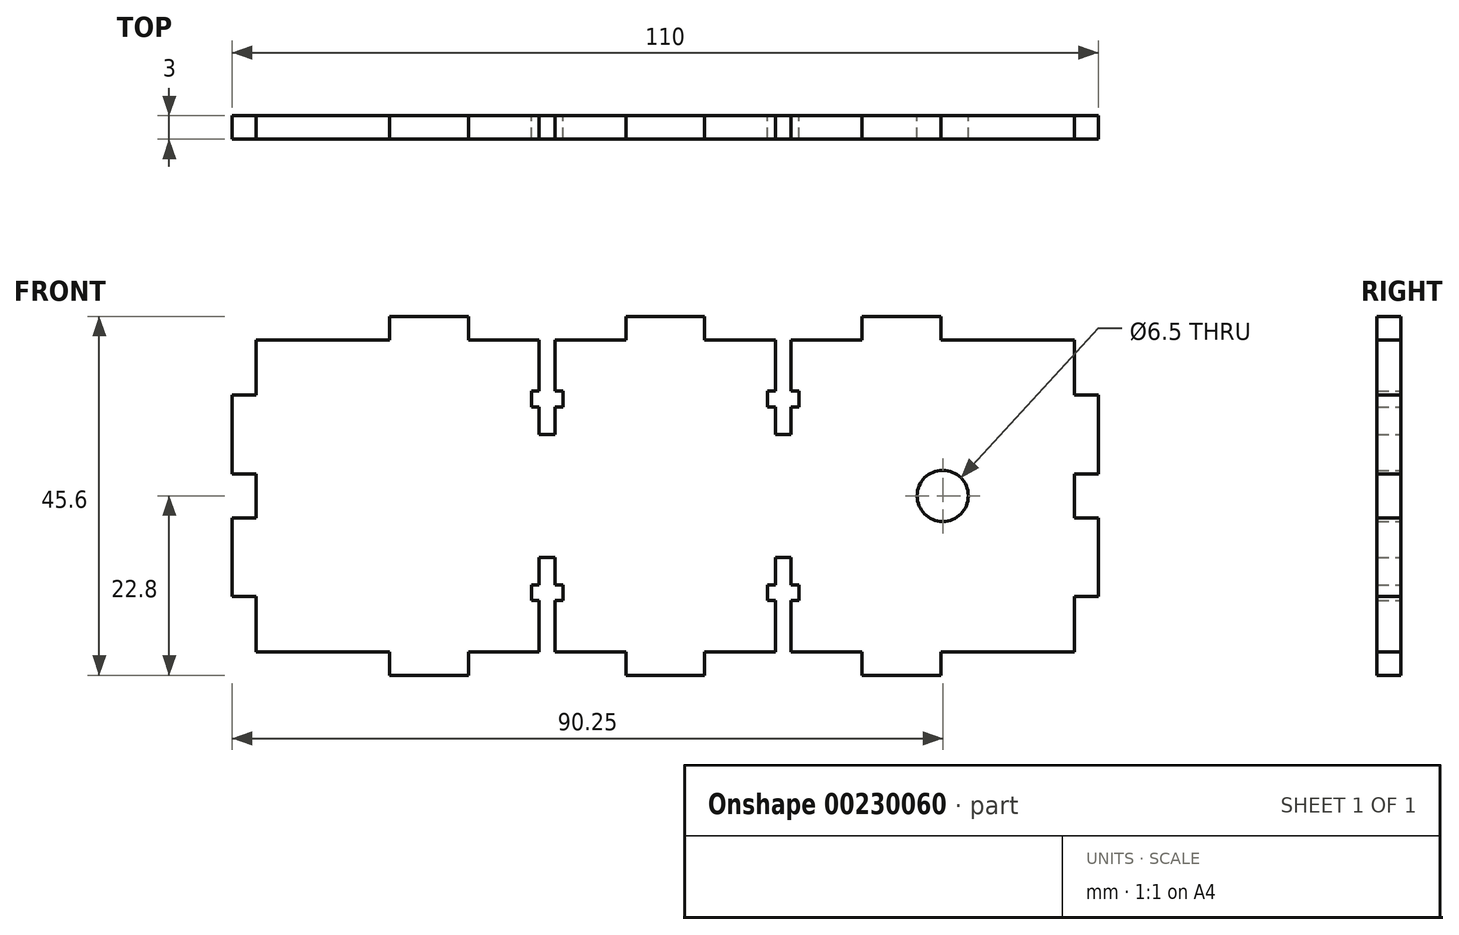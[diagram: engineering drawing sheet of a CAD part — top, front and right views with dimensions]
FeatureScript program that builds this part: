
annotation { "Feature Type Name" : "Feature", "Feature Type Description" : "" }
export const myFeature = defineFeature(function(context is Context, id is Id, definition is map)
    precondition{}
    {
        {
            var Q0;
            Q0=qCreatedBy(makeId("Front.planeOp"),FACE);
            var sketch = newSketch(context, id + "F0", { "sketchPlane" : qUnion([Q0])});
            skLineSegment(sketch, "E0", {"start": v(3, 0) * mm, "end": v(0, 0) * mm});
            skLineSegment(sketch, "E1", {"start": v(3, 0) * mm, "end": v(3, 2.8) * mm});
            skLineSegment(sketch, "E2", {"start": v(3, 2.8) * mm, "end": v(0, 2.8) * mm});
            skLineSegment(sketch, "E3", {"start": v(0, 2.8) * mm, "end": v(0, 12.8) * mm});
            skLineSegment(sketch, "E4", {"start": v(0, 12.8) * mm, "end": v(3, 12.8) * mm});
            skLineSegment(sketch, "E5", {"start": v(3, 12.8) * mm, "end": v(3, 19.8) * mm});
            skLineSegment(sketch, "E6", {"start": v(3, 19.8) * mm, "end": v(20, 19.8) * mm});
            skLineSegment(sketch, "E7", {"start": v(20, 19.8) * mm, "end": v(20, 22.8) * mm});
            skLineSegment(sketch, "E8", {"start": v(20, 22.8) * mm, "end": v(30, 22.8) * mm});
            skLineSegment(sketch, "E9", {"start": v(30, 22.8) * mm, "end": v(30, 19.8) * mm});
            skLineSegment(sketch, "E10", {"start": v(30, 19.8) * mm, "end": v(39, 19.8) * mm});
            skLineSegment(sketch, "E11", {"start": v(50, 19.8) * mm, "end": v(50, 22.8) * mm});
            skLineSegment(sketch, "E12", {"start": v(50, 22.8) * mm, "end": v(55, 22.8) * mm});
            skLineSegment(sketch, "E13", {"start": v(40, 13.3) * mm, "end": v(40, 0) * mm, "construction": true});
            skLineSegment(sketch, "E14.top", {"start": v(39, 7.8) * mm, "end": v(41, 7.8) * mm});
            skLineSegment(sketch, "E14.left", {"start": v(39, 19.8) * mm, "end": v(39, 13.3) * mm});
            skLineSegment(sketch, "E14.right", {"start": v(41, 19.8) * mm, "end": v(41, 13.3) * mm});
            skLineSegment(sketch, "E15.bottom", {"start": v(38, 13.3) * mm, "end": v(39, 13.3) * mm});
            skLineSegment(sketch, "E15.top", {"start": v(38, 11.3) * mm, "end": v(39, 11.3) * mm});
            skLineSegment(sketch, "E15.left", {"start": v(38, 13.3) * mm, "end": v(38, 11.3) * mm});
            skLineSegment(sketch, "E15.right", {"start": v(42, 13.3) * mm, "end": v(42, 11.3) * mm});
            skPoint(sketch, "E16.orphan", {"position": v(40, 19.8) * mm});
            skLineSegment(sketch, "E17.trimOffspring", {"start": v(41, 19.8) * mm, "end": v(50, 19.8) * mm});
            skLineSegment(sketch, "E18.trimOffspring", {"start": v(41, 13.3) * mm, "end": v(42, 13.3) * mm});
            skLineSegment(sketch, "E19.trimOffspring", {"start": v(41, 11.3) * mm, "end": v(41, 7.8) * mm});
            skLineSegment(sketch, "E20.trimOffspring", {"start": v(39, 11.3) * mm, "end": v(39, 7.8) * mm});
            skLineSegment(sketch, "E21.trimOffspring", {"start": v(41, 11.3) * mm, "end": v(42, 11.3) * mm});
            skLineSegment(sketch, "E22", {"start": v(55, 0) * mm, "end": v(3, 0) * mm, "construction": true});
            skLineSegment(sketch, "E23.MirrorCS", {"start": v(38, -11.3) * mm, "end": v(39, -11.3) * mm});
            skLineSegment(sketch, "E24.MirrorCS", {"start": v(41, -13.3) * mm, "end": v(42, -13.3) * mm});
            skLineSegment(sketch, "E25.MirrorCS", {"start": v(41, -11.3) * mm, "end": v(42, -11.3) * mm});
            skLineSegment(sketch, "E26.MirrorCS", {"start": v(38, -13.3) * mm, "end": v(39, -13.3) * mm});
            skLineSegment(sketch, "E27.MirrorCS", {"start": v(39, -7.8) * mm, "end": v(41, -7.8) * mm});
            skLineSegment(sketch, "E28.MirrorCS", {"start": v(3, 0) * mm, "end": v(3, -2.8) * mm});
            skLineSegment(sketch, "E29.MirrorCS", {"start": v(38, -13.3) * mm, "end": v(38, -11.3) * mm});
            skLineSegment(sketch, "E30.MirrorCS", {"start": v(41, -19.8) * mm, "end": v(41, -13.3) * mm});
            skLineSegment(sketch, "E31.MirrorCS", {"start": v(50, -19.8) * mm, "end": v(50, -22.8) * mm});
            skLineSegment(sketch, "E32.MirrorCS", {"start": v(50, -22.8) * mm, "end": v(55, -22.8) * mm});
            skLineSegment(sketch, "E33.MirrorCS", {"start": v(30, -19.8) * mm, "end": v(39, -19.8) * mm});
            skLineSegment(sketch, "E34.MirrorCS", {"start": v(42, -13.3) * mm, "end": v(42, -11.3) * mm});
            skLineSegment(sketch, "E35.MirrorCS", {"start": v(30, -22.8) * mm, "end": v(30, -19.8) * mm});
            skLineSegment(sketch, "E36.MirrorCS", {"start": v(20, -22.8) * mm, "end": v(30, -22.8) * mm});
            skLineSegment(sketch, "E37.MirrorCS", {"start": v(20, -19.8) * mm, "end": v(20, -22.8) * mm});
            skLineSegment(sketch, "E38.MirrorCS", {"start": v(3, -2.8) * mm, "end": v(0, -2.8) * mm});
            skLineSegment(sketch, "E39.MirrorCS", {"start": v(0, -2.8) * mm, "end": v(0, -12.8) * mm});
            skLineSegment(sketch, "E40.MirrorCS", {"start": v(41, -19.8) * mm, "end": v(50, -19.8) * mm});
            skLineSegment(sketch, "E41.MirrorCS", {"start": v(3, -12.8) * mm, "end": v(3, -19.8) * mm});
            skLineSegment(sketch, "E42.MirrorCS", {"start": v(39, -11.3) * mm, "end": v(39, -7.8) * mm});
            skLineSegment(sketch, "E43.MirrorCS", {"start": v(0, -12.8) * mm, "end": v(3, -12.8) * mm});
            skLineSegment(sketch, "E44.MirrorCS", {"start": v(3, -19.8) * mm, "end": v(20, -19.8) * mm});
            skLineSegment(sketch, "E45.MirrorCS", {"start": v(41, -11.3) * mm, "end": v(41, -7.8) * mm});
            skLineSegment(sketch, "E46.MirrorCS", {"start": v(39, -19.8) * mm, "end": v(39, -13.3) * mm});
            skLineSegment(sketch, "E47.MirrorCS", {"start": v(40, -13.3) * mm, "end": v(40, 0) * mm, "construction": true});
            skPoint(sketch, "E48.MirrorP", {"position": v(40, -19.8) * mm});
            skLineSegment(sketch, "E49", {"start": v(55, 22.8) * mm, "end": v(55, -22.8) * mm, "construction": true});
            skLineSegment(sketch, "E50.MirrorCS", {"start": v(72, -13.3) * mm, "end": v(71, -13.3) * mm});
            skLineSegment(sketch, "E51.MirrorCS", {"start": v(72, 13.3) * mm, "end": v(71, 13.3) * mm});
            skLineSegment(sketch, "E52.MirrorCS", {"start": v(72, -13.3) * mm, "end": v(72, -11.3) * mm});
            skLineSegment(sketch, "E53.MirrorCS", {"start": v(71, 7.8) * mm, "end": v(69, 7.8) * mm});
            skLineSegment(sketch, "E54.MirrorCS", {"start": v(107, 0) * mm, "end": v(110, 0) * mm});
            skLineSegment(sketch, "E55.MirrorCS", {"start": v(72, -11.3) * mm, "end": v(71, -11.3) * mm});
            skLineSegment(sketch, "E56.MirrorCS", {"start": v(68, -13.3) * mm, "end": v(68, -11.3) * mm});
            skLineSegment(sketch, "E57.MirrorCS", {"start": v(69, -11.3) * mm, "end": v(68, -11.3) * mm});
            skLineSegment(sketch, "E58.MirrorCS", {"start": v(72, 11.3) * mm, "end": v(71, 11.3) * mm});
            skLineSegment(sketch, "E59.MirrorCS", {"start": v(71, -7.8) * mm, "end": v(69, -7.8) * mm});
            skLineSegment(sketch, "E60.MirrorCS", {"start": v(69, -13.3) * mm, "end": v(68, -13.3) * mm});
            skLineSegment(sketch, "E61.MirrorCS", {"start": v(69, 13.3) * mm, "end": v(68, 13.3) * mm});
            skLineSegment(sketch, "E62.MirrorCS", {"start": v(69, 11.3) * mm, "end": v(68, 11.3) * mm});
            skLineSegment(sketch, "E63.MirrorCS", {"start": v(72, 13.3) * mm, "end": v(72, 11.3) * mm});
            skLineSegment(sketch, "E64.MirrorCS", {"start": v(107, 0) * mm, "end": v(107, 2.8) * mm});
            skLineSegment(sketch, "E65.MirrorCS", {"start": v(90, -19.8) * mm, "end": v(90, -22.8) * mm});
            skLineSegment(sketch, "E66.MirrorCS", {"start": v(55, 0) * mm, "end": v(107, 0) * mm, "construction": true});
            skLineSegment(sketch, "E67.MirrorCS", {"start": v(71, -19.8) * mm, "end": v(71, -13.3) * mm});
            skLineSegment(sketch, "E68.MirrorCS", {"start": v(69, -19.8) * mm, "end": v(69, -13.3) * mm});
            skLineSegment(sketch, "E69.MirrorCS", {"start": v(70, 13.3) * mm, "end": v(70, 0) * mm, "construction": true});
            skLineSegment(sketch, "E70.MirrorCS", {"start": v(71, 19.8) * mm, "end": v(71, 13.3) * mm});
            skLineSegment(sketch, "E71.MirrorCS", {"start": v(107, 2.8) * mm, "end": v(110, 2.8) * mm});
            skPoint(sketch, "E72.MirrorP", {"position": v(70, -19.8) * mm});
            skLineSegment(sketch, "E73.MirrorCS", {"start": v(110, 2.8) * mm, "end": v(110, 12.8) * mm});
            skLineSegment(sketch, "E74.MirrorCS", {"start": v(110, 12.8) * mm, "end": v(107, 12.8) * mm});
            skLineSegment(sketch, "E75.MirrorCS", {"start": v(107, 12.8) * mm, "end": v(107, 19.8) * mm});
            skLineSegment(sketch, "E76.MirrorCS", {"start": v(107, 19.8) * mm, "end": v(90, 19.8) * mm});
            skLineSegment(sketch, "E77.MirrorCS", {"start": v(90, 19.8) * mm, "end": v(90, 22.8) * mm});
            skLineSegment(sketch, "E78.MirrorCS", {"start": v(90, 22.8) * mm, "end": v(80, 22.8) * mm});
            skLineSegment(sketch, "E79.MirrorCS", {"start": v(80, 22.8) * mm, "end": v(80, 19.8) * mm});
            skLineSegment(sketch, "E80.MirrorCS", {"start": v(80, 19.8) * mm, "end": v(71, 19.8) * mm});
            skLineSegment(sketch, "E81.MirrorCS", {"start": v(60, 19.8) * mm, "end": v(60, 22.8) * mm});
            skLineSegment(sketch, "E82.MirrorCS", {"start": v(60, 22.8) * mm, "end": v(55, 22.8) * mm});
            skLineSegment(sketch, "E83.MirrorCS", {"start": v(107, -2.8) * mm, "end": v(110, -2.8) * mm});
            skLineSegment(sketch, "E84.MirrorCS", {"start": v(69, -11.3) * mm, "end": v(69, -7.8) * mm});
            skLineSegment(sketch, "E85.MirrorCS", {"start": v(69, 11.3) * mm, "end": v(69, 7.8) * mm});
            skLineSegment(sketch, "E86.MirrorCS", {"start": v(68, 13.3) * mm, "end": v(68, 11.3) * mm});
            skLineSegment(sketch, "E87.MirrorCS", {"start": v(69, -19.8) * mm, "end": v(60, -19.8) * mm});
            skLineSegment(sketch, "E88.MirrorCS", {"start": v(70, -13.3) * mm, "end": v(70, 0) * mm, "construction": true});
            skLineSegment(sketch, "E89.MirrorCS", {"start": v(107, -19.8) * mm, "end": v(90, -19.8) * mm});
            skLineSegment(sketch, "E90.MirrorCS", {"start": v(69, 19.8) * mm, "end": v(69, 13.3) * mm});
            skLineSegment(sketch, "E91.MirrorCS", {"start": v(60, -19.8) * mm, "end": v(60, -22.8) * mm});
            skLineSegment(sketch, "E92.MirrorCS", {"start": v(107, -12.8) * mm, "end": v(107, -19.8) * mm});
            skLineSegment(sketch, "E93.MirrorCS", {"start": v(60, -22.8) * mm, "end": v(55, -22.8) * mm});
            skPoint(sketch, "E94.MirrorP", {"position": v(70, 19.8) * mm});
            skLineSegment(sketch, "E95.MirrorCS", {"start": v(69, 19.8) * mm, "end": v(60, 19.8) * mm});
            skLineSegment(sketch, "E96.MirrorCS", {"start": v(80, -19.8) * mm, "end": v(71, -19.8) * mm});
            skLineSegment(sketch, "E97.MirrorCS", {"start": v(71, 11.3) * mm, "end": v(71, 7.8) * mm});
            skLineSegment(sketch, "E98.MirrorCS", {"start": v(80, -22.8) * mm, "end": v(80, -19.8) * mm});
            skLineSegment(sketch, "E99.MirrorCS", {"start": v(90, -22.8) * mm, "end": v(80, -22.8) * mm});
            skLineSegment(sketch, "E100.MirrorCS", {"start": v(110, -2.8) * mm, "end": v(110, -12.8) * mm});
            skLineSegment(sketch, "E101.MirrorCS", {"start": v(71, -11.3) * mm, "end": v(71, -7.8) * mm});
            skLineSegment(sketch, "E102.MirrorCS", {"start": v(110, -12.8) * mm, "end": v(107, -12.8) * mm});
            skLineSegment(sketch, "E103.MirrorCS", {"start": v(107, 0) * mm, "end": v(107, -2.8) * mm});
            skCircle(sketch, "E104", {"center": v(90.25, 0) * mm, "radius": 3.25 * mm});
            skSolve(sketch);
        }
        {
            var Q0;
            Q0 = qSketchRegion(id + "F0", true);
            extrude(context, id + "F1", {"entities" : qUnion([Q0]), "depth" : 3 * mm});
        }
    });
